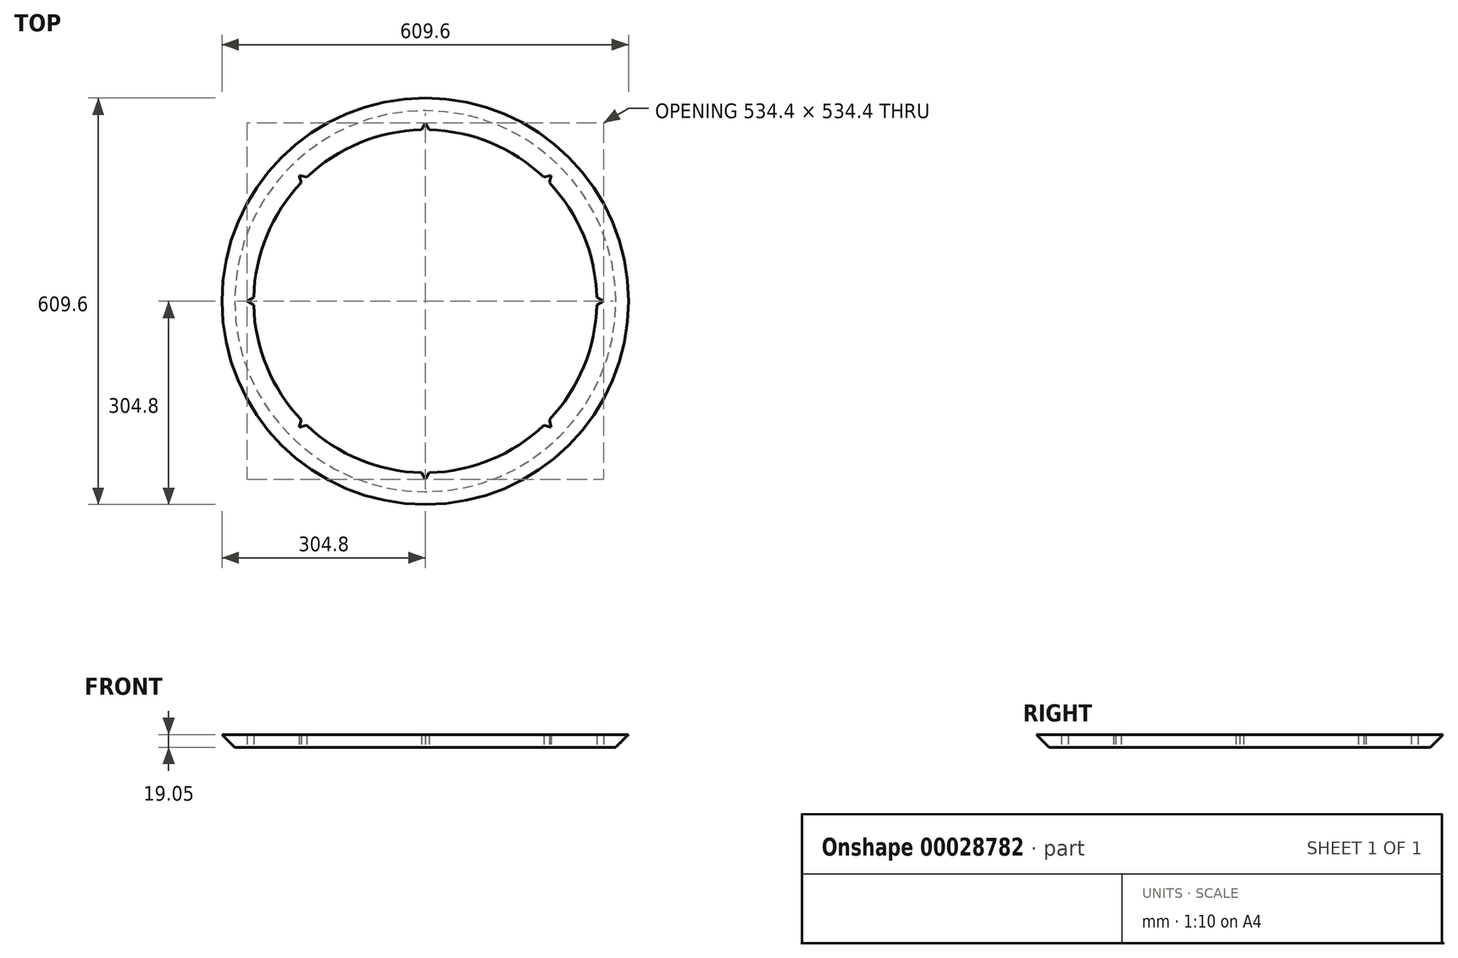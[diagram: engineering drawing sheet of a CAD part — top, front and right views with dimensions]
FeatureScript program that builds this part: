
annotation { "Feature Type Name" : "Feature", "Feature Type Description" : "" }
export const myFeature = defineFeature(function(context is Context, id is Id, definition is map)
    precondition{}
    {
        {
            var Q0;
            Q0=qCreatedBy(makeId("Top.planeOp"),FACE);
            var sketch = newSketch(context, id + "F0", { "sketchPlane" : qUnion([Q0])});
            skCircle(sketch, "E0", {"center": v(0, 0) * mm, "radius": 257.18 * mm});
            skCircle(sketch, "E1", {"center": v(0, 0) * mm, "radius": 304.8 * mm});
            skCircle(sketch, "E2", {"center": v(0, 0) * mm, "radius": 254 * mm, "construction": true});
            skLineSegment(sketch, "E3", {"start": v(0, 0) * mm, "end": v(-254, 0) * mm, "construction": true});
            skLineSegment(sketch, "E4", {"start": v(-254, 62.17) * mm, "end": v(-254, -61.48) * mm, "construction": true});
            skLineSegment(sketch, "E5", {"start": v(-254, 0) * mm, "end": v(-254, 7.62) * mm});
            skLineSegment(sketch, "E6", {"start": v(-254, 7.62) * mm, "end": v(-267.2, 0) * mm});
            skLineSegment(sketch, "E7", {"start": v(-254, 0) * mm, "end": v(-254, -7.62) * mm});
            skLineSegment(sketch, "E8", {"start": v(-267.2, 0) * mm, "end": v(-254, -7.62) * mm});
            skLineSegment(sketch, "E9", {"start": v(0, 257.18) * mm, "end": v(0, -254) * mm, "construction": true});
            skLineSegment(sketch, "E10", {"start": v(0, 0) * mm, "end": v(254, 0) * mm, "construction": true});
            skLineSegment(sketch, "E11", {"start": v(0, 0) * mm, "end": v(181.85, 181.85) * mm, "construction": true});
            skLineSegment(sketch, "E12", {"start": v(0, 0) * mm, "end": v(-179.6, -179.6) * mm, "construction": true});
            skLineSegment(sketch, "E13", {"start": v(0, 0) * mm, "end": v(184.07, -179.6) * mm, "construction": true});
            skLineSegment(sketch, "E14", {"start": v(0, 0) * mm, "end": v(-179.6, 179.6) * mm, "construction": true});
            skLineSegment(sketch, "E15", {"start": v(-179.6, -179.6) * mm, "end": v(-187.28, -171.59) * mm});
            skLineSegment(sketch, "E16.1.0", {"start": v(-188.94, -188.94) * mm, "end": v(-174.22, -185) * mm});
            skLineSegment(sketch, "E16.1.1", {"start": v(-179.6, -179.6) * mm, "end": v(-174.22, -185) * mm});
            skLineSegment(sketch, "E16.1.2", {"start": v(-185, -174.22) * mm, "end": v(-188.94, -188.94) * mm});
            skLineSegment(sketch, "E16.1.3", {"start": v(-179.6, -179.6) * mm, "end": v(-185, -174.22) * mm});
            skLineSegment(sketch, "E16.2.0", {"start": v(0, -267.2) * mm, "end": v(7.62, -254) * mm});
            skLineSegment(sketch, "E16.2.1", {"start": v(0, -254) * mm, "end": v(7.62, -254) * mm});
            skLineSegment(sketch, "E16.2.2", {"start": v(-7.62, -254) * mm, "end": v(0, -267.2) * mm});
            skLineSegment(sketch, "E16.2.3", {"start": v(0, -254) * mm, "end": v(-7.62, -254) * mm});
            skLineSegment(sketch, "E16.3.0", {"start": v(188.94, -188.94) * mm, "end": v(185, -174.22) * mm});
            skLineSegment(sketch, "E16.3.1", {"start": v(179.6, -179.6) * mm, "end": v(185, -174.22) * mm});
            skLineSegment(sketch, "E16.3.2", {"start": v(174.22, -185) * mm, "end": v(188.94, -188.94) * mm});
            skLineSegment(sketch, "E16.3.3", {"start": v(179.6, -179.6) * mm, "end": v(174.22, -185) * mm});
            skLineSegment(sketch, "E16.4.0", {"start": v(267.2, 0) * mm, "end": v(254, 7.62) * mm});
            skLineSegment(sketch, "E16.4.1", {"start": v(254, 0) * mm, "end": v(254, 7.62) * mm});
            skLineSegment(sketch, "E16.4.2", {"start": v(254, -7.62) * mm, "end": v(267.2, 0) * mm});
            skLineSegment(sketch, "E16.4.3", {"start": v(254, 0) * mm, "end": v(254, -7.62) * mm});
            skLineSegment(sketch, "E16.5.0", {"start": v(188.94, 188.94) * mm, "end": v(174.22, 185) * mm});
            skLineSegment(sketch, "E16.5.1", {"start": v(179.6, 179.6) * mm, "end": v(174.22, 185) * mm});
            skLineSegment(sketch, "E16.5.2", {"start": v(185, 174.22) * mm, "end": v(188.94, 188.94) * mm});
            skLineSegment(sketch, "E16.5.3", {"start": v(179.6, 179.6) * mm, "end": v(185, 174.22) * mm});
            skLineSegment(sketch, "E16.6.0", {"start": v(0, 267.2) * mm, "end": v(-7.62, 254) * mm});
            skLineSegment(sketch, "E16.6.1", {"start": v(0, 254) * mm, "end": v(-7.62, 254) * mm});
            skLineSegment(sketch, "E16.6.2", {"start": v(7.62, 254) * mm, "end": v(0, 267.2) * mm});
            skLineSegment(sketch, "E16.6.3", {"start": v(0, 254) * mm, "end": v(7.62, 254) * mm});
            skLineSegment(sketch, "E16.7.0", {"start": v(-188.94, 188.94) * mm, "end": v(-185, 174.22) * mm});
            skLineSegment(sketch, "E16.7.1", {"start": v(-179.6, 179.6) * mm, "end": v(-185, 174.22) * mm});
            skLineSegment(sketch, "E16.7.2", {"start": v(-174.22, 185) * mm, "end": v(-188.94, 188.94) * mm});
            skLineSegment(sketch, "E16.7.3", {"start": v(-179.6, 179.6) * mm, "end": v(-174.22, 185) * mm});
            skSolve(sketch);
        }
        {
            var Q0;
            Q0=makeQuery(id+"F0.imprint","IMPRINT",FACE,{"disambiguationData":[TD([[makeQuery(id+"F0.imprint","IMPRINT",EDGE,{"derivedFrom":sQuery(id+"F0.wireOp",EDGE,"E1")}),1.0]])]});
            extrude(context, id + "F1", {"entities" : qUnion([Q0]), "depth" : 19.05 * mm});
        }
        {
            var Q0;
            Q0=makeQuery(id+"F1.opExtrude","CAP_EDGE",EDGE,{"disambiguationData":[OSD([sQuery(id+"F0.wireOp",EDGE,"E1")])],"isStart":true});
            chamfer(context, id + "F2", {"entities" : qUnion([Q0]), "width" : 19.05 * mm, "tangentPropagation" : true});
        }
    });
